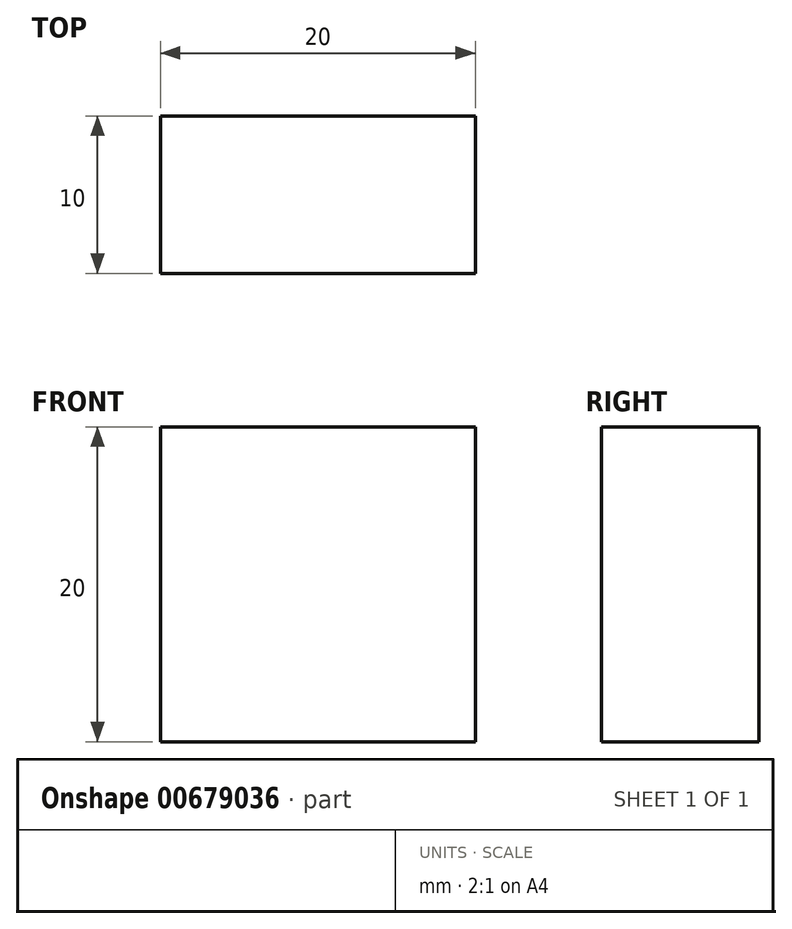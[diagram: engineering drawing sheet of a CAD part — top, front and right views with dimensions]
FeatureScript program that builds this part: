
annotation { "Feature Type Name" : "Feature", "Feature Type Description" : "" }
export const myFeature = defineFeature(function(context is Context, id is Id, definition is map)
    precondition{}
    {
        {
            var Q0;
            Q0=qCreatedBy(makeId("Front.planeOp"),FACE);
            var sketch = newSketch(context, id + "F0", { "sketchPlane" : qUnion([Q0])});
            skLineSegment(sketch, "E0.bottom", {"start": v(0, 0) * mm, "end": v(-20, 0) * mm});
            skLineSegment(sketch, "E0.top", {"start": v(0, 20) * mm, "end": v(-20, 20) * mm});
            skLineSegment(sketch, "E0.left", {"start": v(0, 0) * mm, "end": v(0, 20) * mm});
            skLineSegment(sketch, "E0.right", {"start": v(-20, 0) * mm, "end": v(-20, 20) * mm});
            skSolve(sketch);
        }
        {
            var Q0;
            Q0=makeQuery(id+"F0.imprint","IMPRINT",FACE,{"disambiguationData":[TD([[makeQuery(id+"F0.imprint","IMPRINT",EDGE,{"derivedFrom":sQuery(id+"F0.wireOp",EDGE,"E0.bottom")}),-1.0]])]});
            extrude(context, id + "F1", {"entities" : qUnion([Q0]), "depth" : 10 * mm, "offsetDistance" : 25 * mm});
        }
    });
